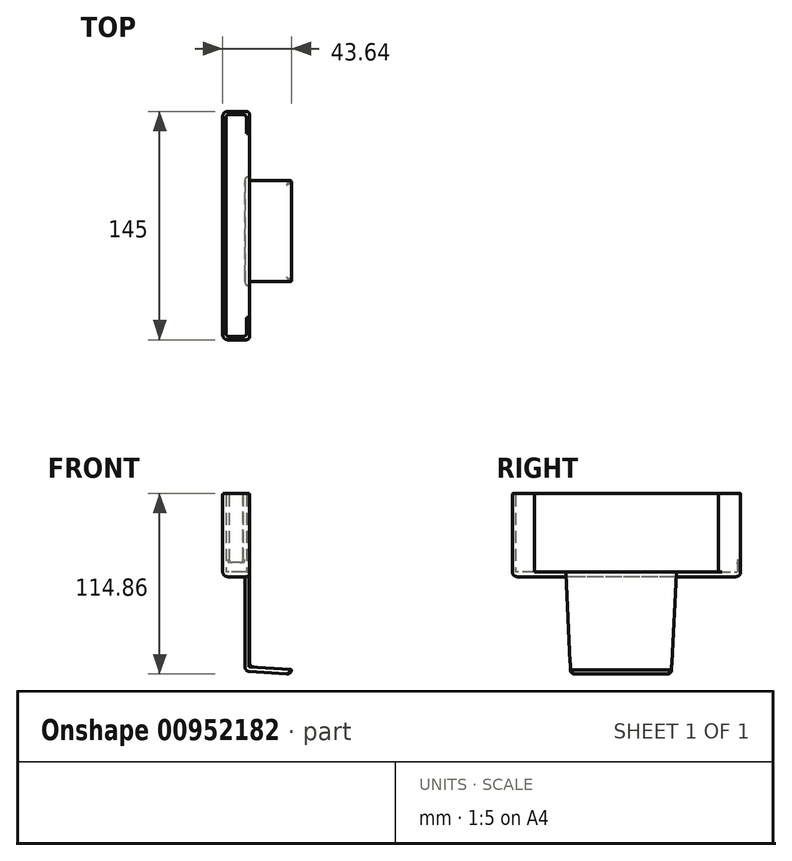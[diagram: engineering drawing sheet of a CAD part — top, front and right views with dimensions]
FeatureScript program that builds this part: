
annotation { "Feature Type Name" : "Feature", "Feature Type Description" : "" }
export const myFeature = defineFeature(function(context is Context, id is Id, definition is map)
    precondition{}
    {
        {
            var Q0;
            Q0=qCreatedBy(makeId("Right.planeOp"),FACE);
            var sketch = newSketch(context, id + "F0", { "sketchPlane" : qUnion([Q0])});
            skLineSegment(sketch, "E0", {"start": v(-35, 0) * mm, "end": v(-32, -60) * mm});
            skLineSegment(sketch, "E1", {"start": v(-32, -60) * mm, "end": v(32, -60) * mm});
            skLineSegment(sketch, "E2", {"start": v(32, -60) * mm, "end": v(35, 0) * mm});
            skLineSegment(sketch, "E3", {"start": v(35, 0) * mm, "end": v(-35, 0) * mm});
            skSolve(sketch);
        }
        {
            var Q0;
            Q0=qSketchRegion(id+"F0",true);
            extrude(context, id + "F1", {"entities" : qUnion([Q0]), "depth" : 3 * mm, "offsetDistance" : 25 * mm});
        }
        {
            var Q0;
            Q0=qCreatedBy(makeId("Right.planeOp"),FACE);
            var sketch = newSketch(context, id + "F2", { "sketchPlane" : qUnion([Q0])});
            skLineSegment(sketch, "E4", {"start": v(-17.69, -60) * mm, "end": v(12.26, -60) * mm, "construction": true});
            skSolve(sketch);
        }
        {
            var Q0;
            Q0=qCreatedBy(makeId("Right.planeOp"),FACE);
            var Q1;
            Q1=sQuery(id+"F2.wireOp",EDGE,"E4");
            cPlane(context, id + "F3", {"entities" : qUnion([Q0, Q1]), "cplaneType" : CPlaneType.LINE_ANGLE, "offset" : 25 * mm, "angle" : 4 * degree, "width" : 150 * mm, "height" : 150 * mm});
        }
        {
            var Q0;
            Q0=qCreatedBy(id+"F3.planeOp",FACE);
            var sketch = newSketch(context, id + "F4", { "sketchPlane" : qUnion([Q0])});
            skLineSegment(sketch, "E5", {"start": v(32, -59.85) * mm, "end": v(-32, -59.85) * mm});
            skLineSegment(sketch, "E6", {"start": v(-32, -59.85) * mm, "end": v(-32.15, -56.85) * mm});
            skLineSegment(sketch, "E7", {"start": v(-32.15, -56.85) * mm, "end": v(32.15, -56.85) * mm});
            skLineSegment(sketch, "E8", {"start": v(32.15, -56.85) * mm, "end": v(32, -59.85) * mm});
            skSolve(sketch);
        }
        {
            var Q0;
            Q0=qSketchRegion(id+"F4",true);
            extrude(context, id + "F5", {"entities" : qUnion([Q0]), "operationType" : NewBodyOperationType.ADD, "oppositeDirection" : true, "depth" : 29.5 * mm, "offsetDistance" : 25 * mm});
        }
        {
            var Q0;
            Q0=qCreatedBy(makeId("Top.planeOp"),FACE);
            var sketch = newSketch(context, id + "F6", { "sketchPlane" : qUnion([Q0])});
            skLineSegment(sketch, "E9", {"start": v(3, 76) * mm, "end": v(-14, 76) * mm});
            skLineSegment(sketch, "E10", {"start": v(-14, 76) * mm, "end": v(-14, -69) * mm});
            skLineSegment(sketch, "E11", {"start": v(3, 76) * mm, "end": v(3, -69) * mm});
            skLineSegment(sketch, "E12", {"start": v(3, -69) * mm, "end": v(-14, -69) * mm});
            skSolve(sketch);
        }
        {
            var Q0;
            Q0=qSketchRegion(id+"F6",true);
            extrude(context, id + "F7", {"entities" : qUnion([Q0]), "operationType" : NewBodyOperationType.ADD, "depth" : 3 * mm, "offsetDistance" : 25 * mm});
        }
        {
            var Q0;
            Q0=makeQuery(id+"F7.opExtrude","CAP_FACE",FACE,{"disambiguationData":[OSD([sQuery(id+"F6.wireOp",EDGE,"E9"),sQuery(id+"F6.wireOp",EDGE,"E10"),sQuery(id+"F6.wireOp",EDGE,"E11"),sQuery(id+"F6.wireOp",EDGE,"E12")])],"isStart":false});
            var sketch = newSketch(context, id + "F8", { "sketchPlane" : qUnion([Q0])});
            skLineSegment(sketch, "E13.left", {"start": v(-14, 76) * mm, "end": v(-14, -69) * mm});
            skLineSegment(sketch, "E14", {"start": v(-14, 76) * mm, "end": v(3, 76) * mm});
            skLineSegment(sketch, "E15", {"start": v(-12, 74) * mm, "end": v(-12, -67) * mm});
            skLineSegment(sketch, "E16", {"start": v(3, -69) * mm, "end": v(-14, -69) * mm});
            skLineSegment(sketch, "E17", {"start": v(3, 76) * mm, "end": v(3, 62) * mm});
            skLineSegment(sketch, "E18", {"start": v(1, 62) * mm, "end": v(1, 74) * mm});
            skLineSegment(sketch, "E19", {"start": v(1, 74) * mm, "end": v(-12, 74) * mm});
            skLineSegment(sketch, "E20", {"start": v(-12, -67) * mm, "end": v(1, -67) * mm});
            skLineSegment(sketch, "E21", {"start": v(1, -67) * mm, "end": v(1, -55) * mm});
            skLineSegment(sketch, "E22", {"start": v(1, -55) * mm, "end": v(3, -55) * mm});
            skLineSegment(sketch, "E23", {"start": v(3, -55) * mm, "end": v(3, -69) * mm});
            skLineSegment(sketch, "E24", {"start": v(1, 62) * mm, "end": v(3, 62) * mm});
            skSolve(sketch);
        }
        {
            var Q0;
            Q0=qSketchRegion(id+"F8",true);
            extrude(context, id + "F9", {"entities" : qUnion([Q0]), "operationType" : NewBodyOperationType.ADD, "depth" : 50 * mm, "offsetDistance" : 25 * mm});
        }
        {
            var Q0;
            Q0=makeQuery(id+"F9.boolean.opBoolean","MERGE",FACE,{"derivedFrom":[makeQuery(id+"F7.opExtrude","SWEPT_FACE",FACE,{"disambiguationData":[OSD([sQuery(id+"F6.wireOp",EDGE,"E9")])]}),makeQuery(id+"F9.opExtrude","SWEPT_FACE",FACE,{"disambiguationData":[OSD([sQuery(id+"F8.wireOp",EDGE,"E14")])]})]});
            var sketch = newSketch(context, id + "F10", { "sketchPlane" : qUnion([Q0])});
            skLineSegment(sketch, "E25.bottom", {"start": v(1, 53) * mm, "end": v(10, 53) * mm});
            skLineSegment(sketch, "E25.top", {"start": v(1, 9) * mm, "end": v(10, 9) * mm});
            skLineSegment(sketch, "E25.left", {"start": v(1, 53) * mm, "end": v(1, 9) * mm});
            skLineSegment(sketch, "E25.right", {"start": v(10, 53) * mm, "end": v(10, 9) * mm});
            skSolve(sketch);
        }
        {
            var Q0;
            Q0=qSketchRegion(id+"F10",true);
            extrude(context, id + "F11", {"entities" : qUnion([Q0]), "operationType" : NewBodyOperationType.REMOVE, "oppositeDirection" : true, "depth" : 5 * mm, "offsetDistance" : 25 * mm});
        }
        {
            var Q0;
            Q0=makeQuery(id+"F5.boolean.opBoolean","MERGE",EDGE,{"derivedFrom":[makeQuery(id+"F1.opExtrude","CAP_EDGE",EDGE,{"disambiguationData":[OSD([sQuery(id+"F0.wireOp",EDGE,"E1")])],"isStart":true}),makeQuery(id+"F5.opExtrude","CAP_EDGE",EDGE,{"disambiguationData":[OSD([sQuery(id+"F4.wireOp",EDGE,"E5")])],"isStart":true})]});
            var Q1;
            Q1=makeQuery(id+"F5.boolean.opBoolean","INTERSECT",EDGE,{"derivedFrom":[makeQuery(id+"F1.opExtrude","CAP_FACE",FACE,{"disambiguationData":[OSD([sQuery(id+"F0.wireOp",EDGE,"E0"),sQuery(id+"F0.wireOp",EDGE,"E1"),sQuery(id+"F0.wireOp",EDGE,"E2"),sQuery(id+"F0.wireOp",EDGE,"E3")])],"isStart":false}),makeQuery(id+"F5.opExtrude","SWEPT_FACE",FACE,{"disambiguationData":[OSD([sQuery(id+"F4.wireOp",EDGE,"E7")])]})]});
            fillet(context, id + "F12", {"entities" : qUnion([Q0, Q1]), "radius" : 3 * mm, "tangentPropagation" : true, "allowEdgeOverflow" : false});
        }
        {
            var Q0;
            Q0=makeQuery(id+"F5.opExtrude","SWEPT_EDGE",EDGE,{"disambiguationData":[OSD([sQuery(id+"F4.wireOp",EDGE,"E5"),sQuery(id+"F4.wireOp",EDGE,"E6")])]});
            var Q1;
            Q1=makeQuery(id+"F5.opExtrude","SWEPT_EDGE",EDGE,{"disambiguationData":[OSD([sQuery(id+"F4.wireOp",EDGE,"E5"),sQuery(id+"F4.wireOp",EDGE,"E8")])]});
            var Q2;
            Q2=makeQuery(id+"F5.opExtrude","CAP_EDGE",EDGE,{"disambiguationData":[OSD([sQuery(id+"F4.wireOp",EDGE,"E5")])],"isStart":false});
            var Q3;
            Q3=makeQuery(id+"F7.opExtrude","CAP_EDGE",EDGE,{"disambiguationData":[OSD([sQuery(id+"F6.wireOp",EDGE,"E12")])],"isStart":true});
            var Q4;
            Q4=makeQuery(id+"F7.opExtrude","CAP_EDGE",EDGE,{"disambiguationData":[OSD([sQuery(id+"F6.wireOp",EDGE,"E9")])],"isStart":true});
            var Q5;
            Q5=makeQuery(id+"F7.opExtrude","CAP_EDGE",EDGE,{"disambiguationData":[OSD([sQuery(id+"F6.wireOp",EDGE,"E10")])],"isStart":true});
            var Q6;
            Q6=makeQuery(id+"F9.boolean.opBoolean","MERGE",EDGE,{"derivedFrom":[makeQuery(id+"F7.opExtrude","SWEPT_EDGE",EDGE,{"disambiguationData":[OSD([sQuery(id+"F6.wireOp",EDGE,"E9"),sQuery(id+"F6.wireOp",EDGE,"E10")])]}),makeQuery(id+"F9.opExtrude","SWEPT_EDGE",EDGE,{"disambiguationData":[OSD([sQuery(id+"F8.wireOp",EDGE,"E13.left"),sQuery(id+"F8.wireOp",EDGE,"E14")])]})]});
            var Q7;
            Q7=makeQuery(id+"F9.boolean.opBoolean","MERGE",EDGE,{"derivedFrom":[makeQuery(id+"F7.opExtrude","SWEPT_EDGE",EDGE,{"disambiguationData":[OSD([sQuery(id+"F6.wireOp",EDGE,"E10"),sQuery(id+"F6.wireOp",EDGE,"E12")])]}),makeQuery(id+"F9.opExtrude","SWEPT_EDGE",EDGE,{"disambiguationData":[OSD([sQuery(id+"F8.wireOp",EDGE,"E13.left"),sQuery(id+"F8.wireOp",EDGE,"E16")])]})]});
            fillet(context, id + "F13", {"entities" : qUnion([Q0, Q1, Q2, Q3, Q4, Q5, Q6, Q7]), "radius" : 3 * mm, "tangentPropagation" : true, "allowEdgeOverflow" : false});
        }
        {
            var Q0;
            Q0=makeQuery(id+"F11.boolean.opBoolean","COPY",EDGE,{"derivedFrom":makeQuery(id+"F11.opExtrude","SWEPT_EDGE",EDGE,{"disambiguationData":[OSD([sQuery(id+"F10.wireOp",EDGE,"E25.top"),sQuery(id+"F10.wireOp",EDGE,"E25.right")])]})});
            var Q1;
            Q1=makeQuery(id+"F11.boolean.opBoolean","COPY",EDGE,{"derivedFrom":makeQuery(id+"F11.opExtrude","SWEPT_EDGE",EDGE,{"disambiguationData":[OSD([sQuery(id+"F10.wireOp",EDGE,"E25.top"),sQuery(id+"F10.wireOp",EDGE,"E25.left")])]})});
            var Q2;
            Q2=makeQuery(id+"F9.opExtrude","CAP_EDGE",EDGE,{"disambiguationData":[OSD([sQuery(id+"F8.wireOp",EDGE,"E15")])],"isStart":true});
            var Q3;
            Q3=makeQuery(id+"F9.opExtrude","CAP_EDGE",EDGE,{"disambiguationData":[OSD([sQuery(id+"F8.wireOp",EDGE,"E19")])],"isStart":true});
            var Q4;
            Q4=makeQuery(id+"F9.opExtrude","SWEPT_EDGE",EDGE,{"disambiguationData":[OSD([sQuery(id+"F6.wireOp",EDGE,"E11"),sQuery(id+"F8.wireOp",EDGE,"E17"),sQuery(id+"F8.wireOp",EDGE,"E24")])]});
            var Q5;
            Q5=makeQuery(id+"F9.opExtrude","CAP_EDGE",EDGE,{"disambiguationData":[OSD([sQuery(id+"F8.wireOp",EDGE,"E18")])],"isStart":true});
            var Q6;
            Q6=makeQuery(id+"F9.opExtrude","CAP_EDGE",EDGE,{"disambiguationData":[OSD([sQuery(id+"F8.wireOp",EDGE,"E24")])],"isStart":true});
            var Q7;
            Q7=makeQuery(id+"F9.opExtrude","CAP_EDGE",EDGE,{"disambiguationData":[OSD([sQuery(id+"F8.wireOp",EDGE,"E22")])],"isStart":true});
            var Q8;
            Q8=makeQuery(id+"F9.opExtrude","CAP_EDGE",EDGE,{"disambiguationData":[OSD([sQuery(id+"F8.wireOp",EDGE,"E20")])],"isStart":true});
            var Q9;
            Q9=makeQuery(id+"F9.opExtrude","CAP_EDGE",EDGE,{"disambiguationData":[OSD([sQuery(id+"F8.wireOp",EDGE,"E21")])],"isStart":true});
            var Q10;
            Q10=makeQuery(id+"F9.opExtrude","SWEPT_EDGE",EDGE,{"disambiguationData":[OSD([sQuery(id+"F8.wireOp",EDGE,"E20"),sQuery(id+"F8.wireOp",EDGE,"E21")])]});
            var Q11;
            Q11=makeQuery(id+"F9.opExtrude","SWEPT_EDGE",EDGE,{"disambiguationData":[OSD([sQuery(id+"F8.wireOp",EDGE,"E15"),sQuery(id+"F8.wireOp",EDGE,"E20")])]});
            var Q12;
            Q12=makeQuery(id+"F9.opExtrude","SWEPT_EDGE",EDGE,{"disambiguationData":[OSD([sQuery(id+"F8.wireOp",EDGE,"E15"),sQuery(id+"F8.wireOp",EDGE,"E19")])]});
            var Q13;
            Q13=makeQuery(id+"F9.opExtrude","SWEPT_EDGE",EDGE,{"disambiguationData":[OSD([sQuery(id+"F8.wireOp",EDGE,"E18"),sQuery(id+"F8.wireOp",EDGE,"E19")])]});
            var Q14;
            Q14=makeQuery(id+"F9.boolean.opBoolean","MERGE",EDGE,{"derivedFrom":[makeQuery(id+"F7.opExtrude","SWEPT_EDGE",EDGE,{"disambiguationData":[OSD([sQuery(id+"F6.wireOp",EDGE,"E11"),sQuery(id+"F6.wireOp",EDGE,"E12")])]}),makeQuery(id+"F9.opExtrude","SWEPT_EDGE",EDGE,{"disambiguationData":[OSD([sQuery(id+"F8.wireOp",EDGE,"E16"),sQuery(id+"F8.wireOp",EDGE,"E23")])]})]});
            fillet(context, id + "F14", {"entities" : qUnion([Q0, Q1, Q2, Q3, Q4, Q5, Q6, Q7, Q8, Q9, Q10, Q11, Q12, Q13, Q14]), "radius" : 2 * mm, "tangentPropagation" : true, "allowEdgeOverflow" : false});
        }
        {
            var Q0;
            Q0=makeQuery(id+"F11.boolean.opBoolean","COPY",EDGE,{"derivedFrom":makeQuery(id+"F11.opExtrude","CAP_EDGE",EDGE,{"disambiguationData":[OSD([sQuery(id+"F10.wireOp",EDGE,"E25.left")])],"isStart":true})});
            var Q1;
            Q1=makeQuery(id+"F14.opFillet","BLEND_EDGE",EDGE,{"blendedFrom":[makeQuery(id+"F9.opExtrude","SWEPT_EDGE",EDGE,{"disambiguationData":[OSD([sQuery(id+"F8.wireOp",EDGE,"E15"),sQuery(id+"F8.wireOp",EDGE,"E19")])]}),makeQuery(id+"F11.boolean.opBoolean","COPY",FACE,{"derivedFrom":makeQuery(id+"F11.opExtrude","SWEPT_FACE",FACE,{"disambiguationData":[OSD([sQuery(id+"F10.wireOp",EDGE,"E25.right")])]})})],"blendedInto":[makeQuery(id+"F11.boolean.opBoolean","COPY",FACE,{"derivedFrom":makeQuery(id+"F11.opExtrude","SWEPT_FACE",FACE,{"disambiguationData":[OSD([sQuery(id+"F10.wireOp",EDGE,"E25.right")])]})})]});
            var Q2;
            Q2=makeQuery(id+"F9.opExtrude","CAP_EDGE",EDGE,{"disambiguationData":[OSD([sQuery(id+"F8.wireOp",EDGE,"E17")])],"isStart":false});
            var Q3;
            Q3=makeQuery(id+"F9.opExtrude","CAP_EDGE",EDGE,{"disambiguationData":[OSD([sQuery(id+"F8.wireOp",EDGE,"E18")])],"isStart":false});
            var Q4;
            {var subQ2=sQuery(id+"F8.wireOp",EDGE,"E14");Q4=makeQuery(id+"F11.boolean.opBoolean","SPLIT",EDGE,{"disambiguationData":[TD([makeQuery(id+"F7.opExtrude","SWEPT_FACE",FACE,{"disambiguationData":[OSD([sQuery(id+"F6.wireOp",EDGE,"E11")])]})])],"derivedFrom":makeQuery(id+"F9.opExtrude","CAP_EDGE",EDGE,{"disambiguationData":[OSD([subQ2])],"isStart":false})});}
            var Q5;
            Q5=makeQuery(id+"F9.opExtrude","CAP_EDGE",EDGE,{"disambiguationData":[OSD([sQuery(id+"F8.wireOp",EDGE,"E13.left")])],"isStart":false});
            var Q6;
            Q6=makeQuery(id+"F9.opExtrude","CAP_EDGE",EDGE,{"disambiguationData":[OSD([sQuery(id+"F8.wireOp",EDGE,"E15")])],"isStart":false});
            var Q7;
            Q7=makeQuery(id+"F11.boolean.opBoolean","COPY",EDGE,{"derivedFrom":makeQuery(id+"F11.opExtrude","SWEPT_EDGE",EDGE,{"disambiguationData":[OSD([sQuery(id+"F8.wireOp",EDGE,"E14"),sQuery(id+"F10.wireOp",EDGE,"E25.bottom"),sQuery(id+"F10.wireOp",EDGE,"E25.right")])]})});
            fillet(context, id + "F15", {"entities" : qUnion([Q0, Q1, Q2, Q3, Q4, Q5, Q6, Q7]), "radius" : 1 * mm, "tangentPropagation" : true, "allowEdgeOverflow" : false});
        }
        {
            var Q0;
            Q0=makeQuery(id+"F9.boolean.opBoolean","MERGE",EDGE,{"derivedFrom":[makeQuery(id+"F7.opExtrude","SWEPT_EDGE",EDGE,{"disambiguationData":[OSD([sQuery(id+"F6.wireOp",EDGE,"E9"),sQuery(id+"F6.wireOp",EDGE,"E11")])]}),makeQuery(id+"F9.opExtrude","SWEPT_EDGE",EDGE,{"disambiguationData":[OSD([sQuery(id+"F8.wireOp",EDGE,"E14"),sQuery(id+"F8.wireOp",EDGE,"E17")])]})]});
            fillet(context, id + "F16", {"entities" : qUnion([Q0]), "radius" : 2 * mm, "tangentPropagation" : true, "allowEdgeOverflow" : false});
        }
        {
            var Q0;
            {var subQ0=sQuery(id+"F4.wireOp",EDGE,"E5");Q0=makeQuery(id+"F13.opFillet","BLEND_EDGE",EDGE,{"blendedFrom":[makeQuery(id+"F5.opExtrude","CAP_EDGE",EDGE,{"disambiguationData":[OSD([subQ0])],"isStart":false}),makeQuery(id+"F5.opExtrude","SWEPT_EDGE",EDGE,{"disambiguationData":[OSD([subQ0,sQuery(id+"F4.wireOp",EDGE,"E8")])]})],"blendedInto":[]});}
            var Q1;
            {var subQ0=sQuery(id+"F4.wireOp",EDGE,"E5");Q1=makeQuery(id+"F13.opFillet","BLEND_EDGE",EDGE,{"blendedFrom":[makeQuery(id+"F5.opExtrude","CAP_EDGE",EDGE,{"disambiguationData":[OSD([subQ0])],"isStart":false}),makeQuery(id+"F5.opExtrude","SWEPT_EDGE",EDGE,{"disambiguationData":[OSD([subQ0,sQuery(id+"F4.wireOp",EDGE,"E6")])]})],"blendedInto":[]});}
            fillet(context, id + "F17", {"entities" : qUnion([Q0, Q1]), "radius" : 1 * mm, "tangentPropagation" : true, "allowEdgeOverflow" : false});
        }
    });
